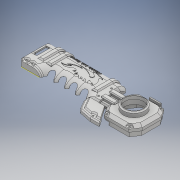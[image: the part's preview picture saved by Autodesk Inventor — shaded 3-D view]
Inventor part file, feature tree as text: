
AUTODESK INVENTOR PART (.ipt)
format: ipt  version: 2018 (Build 220112000, 112)  size: 5,953,536 bytes
history: native  units: mm
features: extrude x10, sketch x10, other x5, projected_geometry x5
ambient origin geometry x8: Origin, YZ Plane, XZ Plane, XY Plane, X Axis, Y Axis, Z Axis, Center Point
bodies: Body1 (feature_tree)
feature tree (30):
  other  "undercover_modified.ipt"
  extrude  "押し出し2"  Depth=10.0mm
  extrude  "押し出し3"  Depth=20.5mm TaperAngle=0.0deg
  extrude  "押し出し4"  Depth=20.5mm TaperAngle=0.0deg
  extrude  "押し出し5"  TaperAngle=60.0deg  [1 undecoded]
  extrude  "押し出し6"  Depth=10.0mm TaperAngle=0.0deg
  extrude  "押し出し7"  Depth=5.0mm
  extrude  "押し出し8"  Depth=4.0mm
  extrude  "押し出し9"  Depth=6.5mm
  extrude  "押し出し10"  Depth=5.0mm TaperAngle=0.0deg
  extrude  "押し出し11"  Depth=5.0mm TaperAngle=0.0deg
  other  "ソリッド1::undercover_modified.ipt"
  other  "TaggingFeature1"
  other  "作業平面1"
  sketch  "スケッチ5"
  sketch  "スケッチ6"
  projected_geometry  "投影ループ19"
  projected_geometry  "投影ループ20"
  projected_geometry  "投影ループ21"
  sketch  "スケッチ7"
  sketch  "スケッチ8"
  sketch  "スケッチ9"
  sketch  "スケッチ10"
  sketch  "スケッチ11"
  sketch  "スケッチ12"
  projected_geometry  "投影ループ22"
  sketch  "スケッチ13"
  projected_geometry  "投影ループ23"
  sketch  "スケッチ14"
  other  "ソリッド1"
note: 1 required parameter value undecoded (feature->parameter linkage not recoverable at this tier; creation-order binding heuristic only, values carry confidence <= 0.55)
